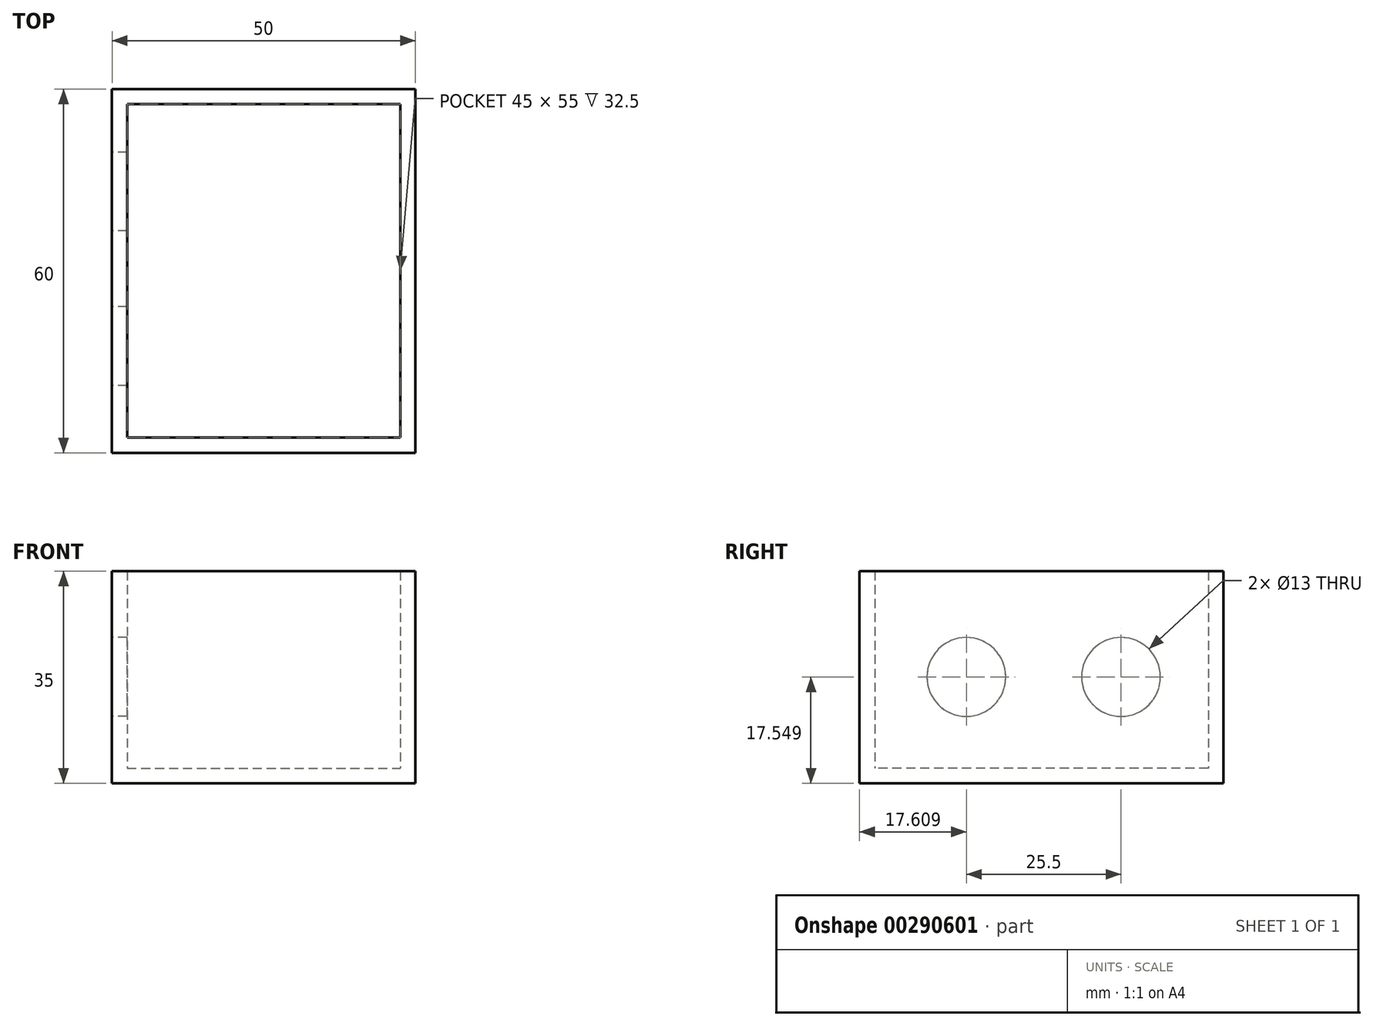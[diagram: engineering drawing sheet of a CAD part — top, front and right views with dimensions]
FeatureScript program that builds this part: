
annotation { "Feature Type Name" : "Feature", "Feature Type Description" : "" }
export const myFeature = defineFeature(function(context is Context, id is Id, definition is map)
    precondition{}
    {
        {
            var Q0;
            Q0=qCreatedBy(makeId("Top.planeOp"),FACE);
            var sketch = newSketch(context, id + "F0", { "sketchPlane" : qUnion([Q0])});
            skLineSegment(sketch, "E0.bottom", {"start": v(-49.82, 60.18) * mm, "end": v(0.18, 60.18) * mm});
            skLineSegment(sketch, "E0.top", {"start": v(-49.82, 0.18) * mm, "end": v(0.18, 0.18) * mm});
            skLineSegment(sketch, "E0.left", {"start": v(-49.82, 60.18) * mm, "end": v(-49.82, 0.18) * mm});
            skLineSegment(sketch, "E0.right", {"start": v(0.18, 60.18) * mm, "end": v(0.18, 0.18) * mm});
            skLineSegment(sketch, "E1.top", {"start": v(-49.82, 2.68) * mm, "end": v(0.18, 2.68) * mm});
            skLineSegment(sketch, "E1.left", {"start": v(-49.82, 0.18) * mm, "end": v(-49.82, 2.68) * mm});
            skLineSegment(sketch, "E1.right", {"start": v(0.18, 0.18) * mm, "end": v(0.18, 2.68) * mm});
            skLineSegment(sketch, "E2.top", {"start": v(-49.82, 57.68) * mm, "end": v(0.18, 57.68) * mm});
            skLineSegment(sketch, "E2.left", {"start": v(-49.82, 60.18) * mm, "end": v(-49.82, 57.68) * mm});
            skLineSegment(sketch, "E2.right", {"start": v(0.18, 60.18) * mm, "end": v(0.18, 57.68) * mm});
            skLineSegment(sketch, "E3.bottom", {"start": v(-49.82, 57.68) * mm, "end": v(-47.32, 57.68) * mm});
            skLineSegment(sketch, "E3.top", {"start": v(-49.82, 2.68) * mm, "end": v(-47.32, 2.68) * mm});
            skLineSegment(sketch, "E3.left", {"start": v(-49.82, 57.68) * mm, "end": v(-49.82, 2.68) * mm});
            skLineSegment(sketch, "E3.right", {"start": v(-47.32, 57.68) * mm, "end": v(-47.32, 2.68) * mm});
            skLineSegment(sketch, "E4.bottom", {"start": v(0.18, 57.68) * mm, "end": v(-2.32, 57.68) * mm});
            skLineSegment(sketch, "E4.top", {"start": v(0.18, 2.68) * mm, "end": v(-2.32, 2.68) * mm});
            skLineSegment(sketch, "E4.left", {"start": v(0.18, 57.68) * mm, "end": v(0.18, 2.68) * mm});
            skLineSegment(sketch, "E4.right", {"start": v(-2.32, 57.68) * mm, "end": v(-2.32, 2.68) * mm});
            skSolve(sketch);
        }
        {
            var Q0;
            {var subQ4=sQuery(id+"F0.wireOp",EDGE,"E0.top");Q0=makeQuery(id+"F0.imprint","IMPRINT",FACE,{"disambiguationData":[TD([[makeQuery(id+"F0.imprint","IMPRINT",EDGE,{"derivedFrom":subQ4}),1.0]])]});}
            var Q1;
            {var subQ5=sQuery(id+"F0.wireOp",EDGE,"E3.right");Q1=makeQuery(id+"F0.imprint","IMPRINT",FACE,{"disambiguationData":[TD([[makeQuery(id+"F0.imprint","IMPRINT",EDGE,{"derivedFrom":subQ5}),-1.0]])]});}
            var Q2;
            {var subQ3=sQuery(id+"F0.wireOp",EDGE,"E0.bottom");Q2=makeQuery(id+"F0.imprint","IMPRINT",FACE,{"disambiguationData":[TD([[makeQuery(id+"F0.imprint","IMPRINT",EDGE,{"derivedFrom":subQ3}),-1.0]])]});}
            var Q3;
            {var subQ5=sQuery(id+"F0.wireOp",EDGE,"E4.right");Q3=makeQuery(id+"F0.imprint","IMPRINT",FACE,{"disambiguationData":[TD([[makeQuery(id+"F0.imprint","IMPRINT",EDGE,{"derivedFrom":subQ5}),1.0]])]});}
            extrude(context, id + "F1", {"entities" : qUnion([Q0, Q1, Q2, Q3]), "depth" : 35 * mm, "offsetDistance" : 25 * mm});
        }
        {
            var Q0;
            {var subQ0=sQuery(id+"F0.wireOp",EDGE,"E3.right");Q0=makeQuery(id+"F0.imprint","IMPRINT",FACE,{"disambiguationData":[TD([[makeQuery(id+"F0.imprint","IMPRINT",EDGE,{"derivedFrom":subQ0}),1.0]])]});}
            extrude(context, id + "F2", {"entities" : qUnion([Q0]), "operationType" : NewBodyOperationType.ADD, "depth" : 2.5 * mm, "offsetDistance" : 25 * mm});
        }
        {
            var Q0;
            Q0=makeQuery(id+"F1.opExtrude","SWEPT_FACE",FACE,{"disambiguationData":[OSD([sQuery(id+"F0.wireOp",EDGE,"E0.left")])]});
            var sketch = newSketch(context, id + "F3", { "sketchPlane" : qUnion([Q0])});
            skPoint(sketch, "E5", {"position": v(-43.29, 17.55) * mm});
            skPoint(sketch, "E6", {"position": v(-17.79, 17.55) * mm});
            skSolve(sketch);
        }
        {
            var Q0;
            Q0=sQuery(id+"F3.wireOp",VERTEX,"E5");
            var Q1;
            Q1=makeQuery(id+"F1.opExtrude","SWEPT_BODY",BODY,{"disambiguationData":[OSD([sQuery(id+"F0.wireOp",EDGE,"E0.bottom"),sQuery(id+"F0.wireOp",EDGE,"E0.top"),sQuery(id+"F0.wireOp",EDGE,"E0.left"),sQuery(id+"F0.wireOp",EDGE,"E0.right"),sQuery(id+"F0.wireOp",EDGE,"E1.top"),sQuery(id+"F0.wireOp",EDGE,"E2.top"),sQuery(id+"F0.wireOp",EDGE,"E3.right"),sQuery(id+"F0.wireOp",EDGE,"E4.right")])]});
            hole(context, id + "F4", {"style" : HoleStyle.SIMPLE, "endStyle" : HoleEndStyle.BLIND, "holeDiameter" : 13 * mm, "majorDiameter" : 5 * mm, "holeDepth" : 12 * mm, "isTappedThrough" : true, "tappedDepth" : 12 * mm, "tapClearance" : 3, "locations" : qUnion([Q0]), "scope" : qUnion([Q1])});
        }
        {
            var Q0;
            Q0=sQuery(id+"F3.wireOp",VERTEX,"E6");
            var Q1;
            Q1=makeQuery(id+"F1.opExtrude","SWEPT_BODY",BODY,{"disambiguationData":[OSD([sQuery(id+"F0.wireOp",EDGE,"E0.bottom"),sQuery(id+"F0.wireOp",EDGE,"E0.top"),sQuery(id+"F0.wireOp",EDGE,"E0.left"),sQuery(id+"F0.wireOp",EDGE,"E0.right"),sQuery(id+"F0.wireOp",EDGE,"E1.top"),sQuery(id+"F0.wireOp",EDGE,"E2.top"),sQuery(id+"F0.wireOp",EDGE,"E3.right"),sQuery(id+"F0.wireOp",EDGE,"E4.right")])]});
            hole(context, id + "F5", {"style" : HoleStyle.SIMPLE, "endStyle" : HoleEndStyle.BLIND, "holeDiameter" : 13 * mm, "majorDiameter" : 5 * mm, "holeDepth" : 12 * mm, "isTappedThrough" : true, "tappedDepth" : 12 * mm, "tapClearance" : 3, "locations" : qUnion([Q0]), "scope" : qUnion([Q1])});
        }
    });
